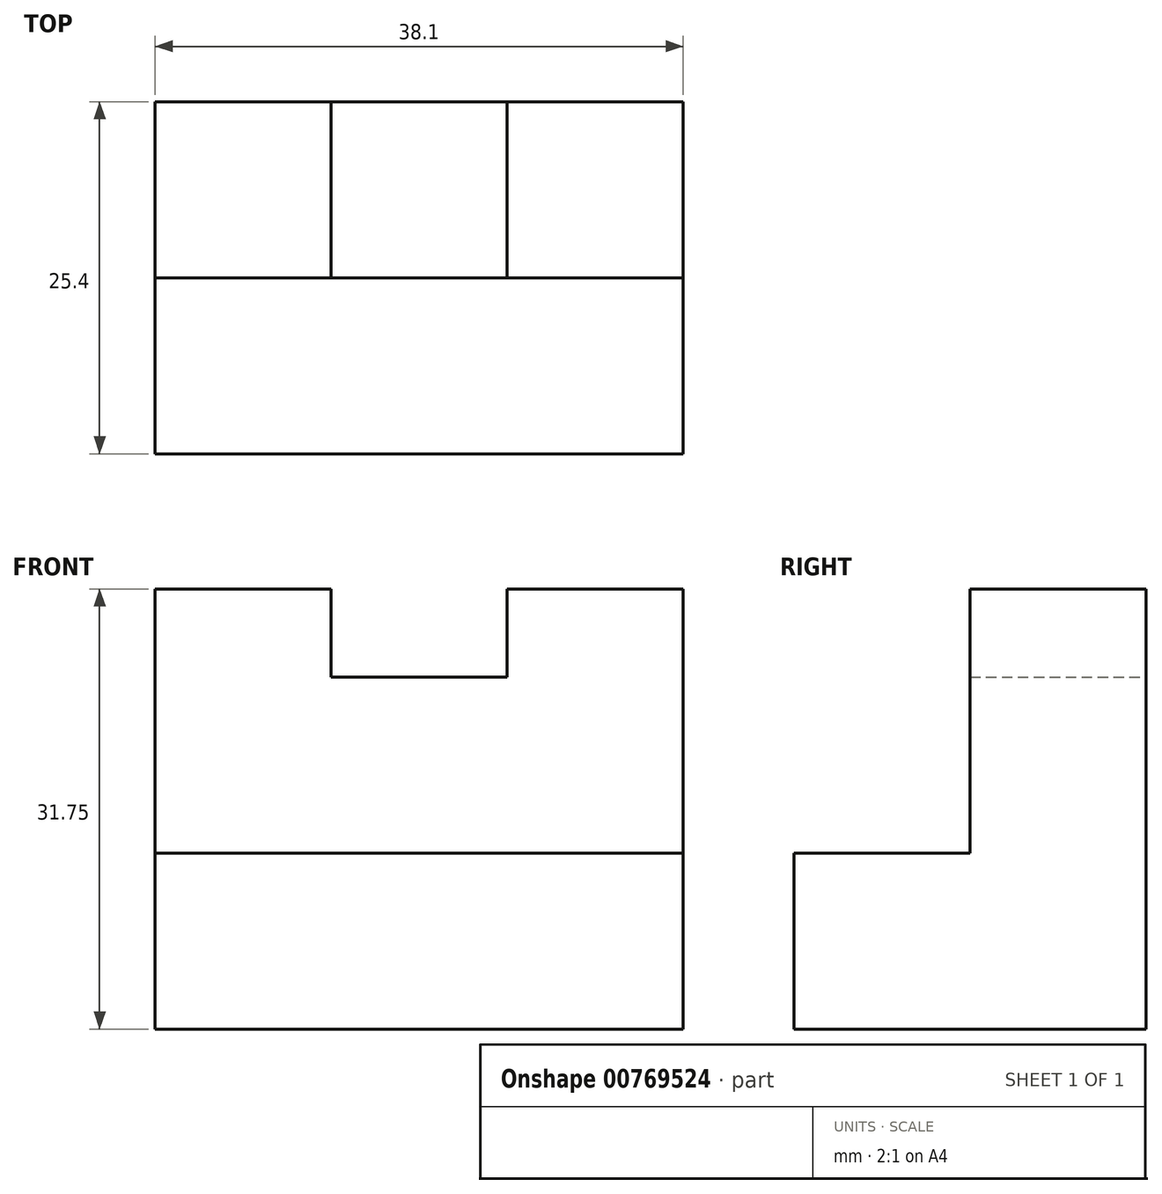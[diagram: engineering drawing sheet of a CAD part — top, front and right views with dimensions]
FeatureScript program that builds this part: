
annotation { "Feature Type Name" : "Feature", "Feature Type Description" : "" }
export const myFeature = defineFeature(function(context is Context, id is Id, definition is map)
    precondition{}
    {
        {
            var Q0;
            Q0=qCreatedBy(makeId("Front.planeOp"),FACE);
            var sketch = newSketch(context, id + "F0", { "sketchPlane" : qUnion([Q0])});
            skLineSegment(sketch, "E0", {"start": v(0, 0) * mm, "end": v(0, -31.75) * mm});
            skLineSegment(sketch, "E1", {"start": v(0, -31.75) * mm, "end": v(38.1, -31.75) * mm});
            skLineSegment(sketch, "E2", {"start": v(38.1, -31.75) * mm, "end": v(38.1, 0) * mm});
            skLineSegment(sketch, "E3", {"start": v(38.1, 0) * mm, "end": v(25.4, 0) * mm});
            skLineSegment(sketch, "E4", {"start": v(25.4, 0) * mm, "end": v(25.4, -6.35) * mm});
            skLineSegment(sketch, "E5", {"start": v(25.4, -6.35) * mm, "end": v(12.7, -6.35) * mm});
            skLineSegment(sketch, "E6", {"start": v(12.7, -6.35) * mm, "end": v(12.7, 0) * mm});
            skLineSegment(sketch, "E7", {"start": v(12.7, 0) * mm, "end": v(0, 0) * mm});
            skSolve(sketch);
        }
        {
            var Q0;
            Q0 = qSketchRegion(id + "F0", true);
            extrude(context, id + "F1", {"entities" : qUnion([Q0]), "depth" : 25.4 * mm, "offsetDistance" : 25.4 * mm});
        }
        {
            var Q0;
            Q0=makeQuery(id+"F1.opExtrude","SWEPT_FACE",FACE,{"disambiguationData":[OSD([sQuery(id+"F0.wireOp",EDGE,"E2")])]});
            var sketch = newSketch(context, id + "F2", { "sketchPlane" : qUnion([Q0])});
            skLineSegment(sketch, "E8", {"start": v(-25.4, -31.75) * mm, "end": v(-25.4, -19.05) * mm});
            skLineSegment(sketch, "E9", {"start": v(-25.4, -19.05) * mm, "end": v(-12.7, -19.05) * mm});
            skLineSegment(sketch, "E10", {"start": v(-12.7, -19.05) * mm, "end": v(-12.7, 0) * mm});
            skSolve(sketch);
        }
        {
            var Q0;
            {var subQ0=sQuery(id+"F2.wireOp",EDGE,"E9");Q0=makeQuery(id+"F2.imprint","IMPRINT",FACE,{"disambiguationData":[TD([[makeQuery(id+"F2.imprint","IMPRINT",EDGE,{"derivedFrom":subQ0}),1.0]])]});}
            extrude(context, id + "F3", {"entities" : qUnion([Q0]), "operationType" : NewBodyOperationType.REMOVE, "oppositeDirection" : true, "depth" : 38.1 * mm, "offsetDistance" : 25.4 * mm});
        }
    });
